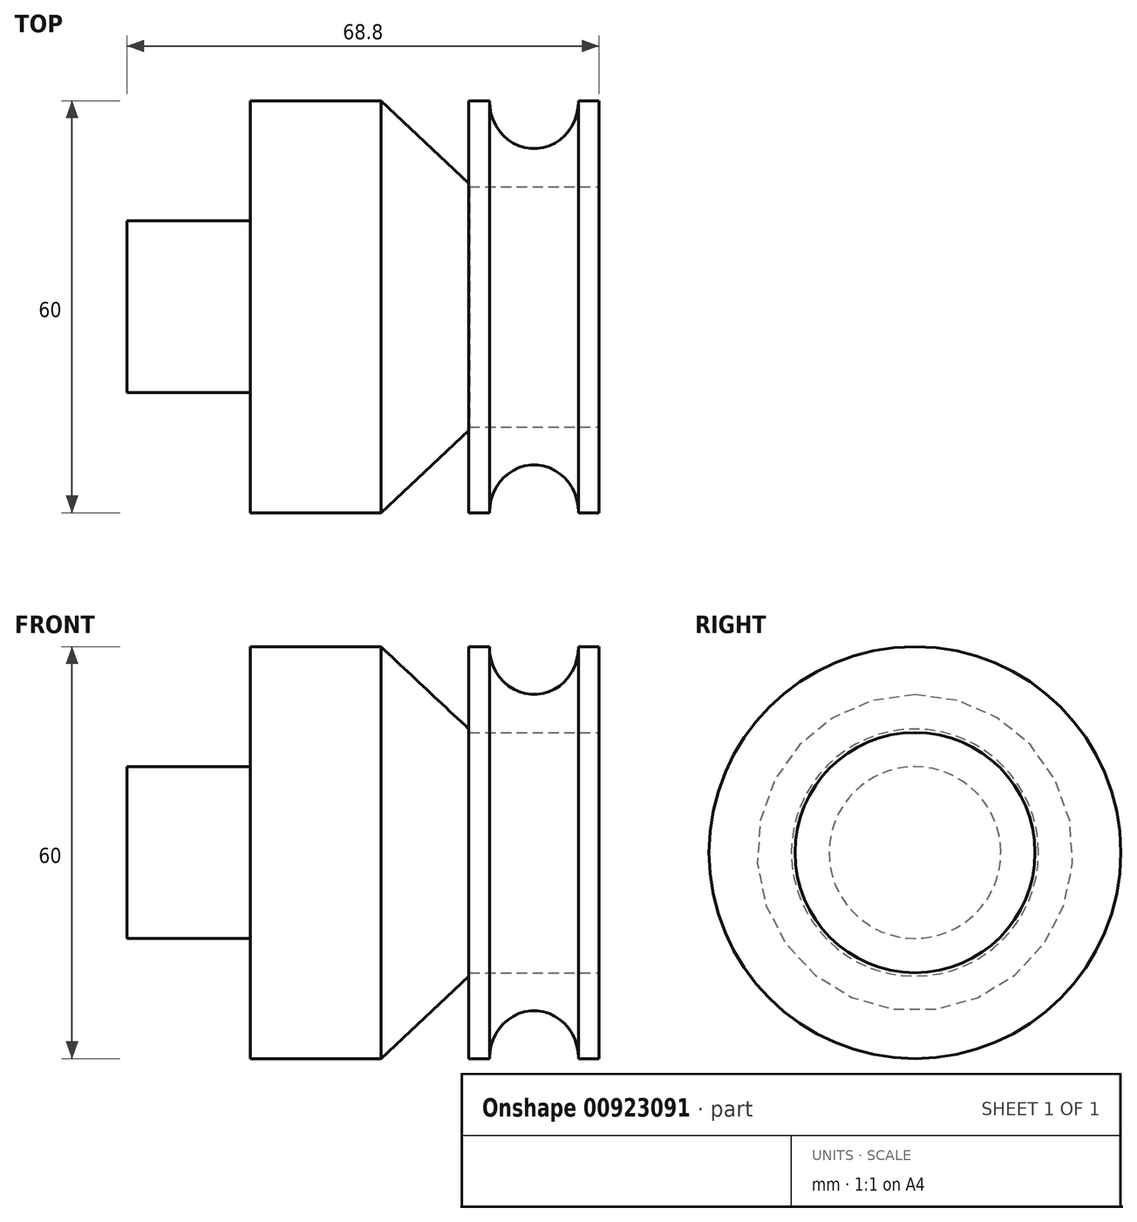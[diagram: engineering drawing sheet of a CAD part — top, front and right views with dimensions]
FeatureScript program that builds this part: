
annotation { "Feature Type Name" : "Feature", "Feature Type Description" : "" }
export const myFeature = defineFeature(function(context is Context, id is Id, definition is map)
    precondition{}
    {
        {
            var Q0;
            Q0=qCreatedBy(makeId("Front.planeOp"),FACE);
            var sketch = newSketch(context, id + "F0", { "sketchPlane" : qUnion([Q0])});
            skLineSegment(sketch, "E0", {"start": v(-12.2, 0) * mm, "end": v(-12.2, 30) * mm});
            skLineSegment(sketch, "E1", {"start": v(6.8, 0) * mm, "end": v(6.8, 30) * mm});
            skLineSegment(sketch, "E2", {"start": v(-12.2, 30) * mm, "end": v(-9.2, 30) * mm});
            skLineSegment(sketch, "E3", {"start": v(6.8, 30) * mm, "end": v(3.8, 30) * mm});
            skLineSegment(sketch, "E4", {"start": v(-12.2, 0) * mm, "end": v(6.8, 0) * mm});
            skPoint(sketch, "E5.centerSnap0", {"position": v(-2.7, 0) * mm});
            skEllipticalArc(sketch, "E6", {});
            const initialGuessF0  = {"E6": [-0.0026993720531463625, 0.03, 0, -1, 0.006985, 0.0065, 4.71238898038469, 1.5707963267948966]};
            skSetInitialGuess(sketch, initialGuessF0);
            skSolve(sketch);
        }
        {
            var Q0;
            Q0 = qSketchRegion(id + "F0", true);
            var Q1;
            Q1=sQuery(id+"F0.wireOp",EDGE,"E4");
            revolve(context, id + "F1", {"surfaceOperationType" : NewSurfaceOperationType.NEW, "entities" : qUnion([Q0]), "axis" : qUnion([Q1]), "revolveType" : RevolveType.FULL});
        }
        {
            var Q0;
            Q0=makeQuery(id+"F1.opRevolve","SWEPT_FACE",FACE,{"disambiguationData":[OSD([sQuery(id+"F0.wireOp",EDGE,"E1")])]});
            var sketch = newSketch(context, id + "F2", { "sketchPlane" : qUnion([Q0])});
            skCircle(sketch, "E7", {"center": v(0, 0) * mm, "radius": 17.48 * mm});
            skSolve(sketch);
        }
        {
            var Q0;
            Q0=makeQuery(id+"F2.imprint","IMPRINT",FACE,{"disambiguationData":[TD([[makeQuery(id+"F2.imprint","IMPRINT",EDGE,{"derivedFrom":sQuery(id+"F2.wireOp",EDGE,"E7")}),1.0]])]});
            var Q1;
            Q1=makeQuery(id+"F1.opRevolve","SWEPT_FACE",FACE,{"disambiguationData":[OSD([sQuery(id+"F0.wireOp",EDGE,"E0")])]});
            extrude(context, id + "F3", {"entities" : qUnion([Q0]), "operationType" : NewBodyOperationType.REMOVE, "oppositeDirection" : true, "depth" : 18.9 * mm, "endBoundEntityFace" : qUnion([Q1]), "offsetDistance" : 25 * mm});
        }
        {
            var Q0;
            Q0=makeQuery(id+"F1.opRevolve","SWEPT_FACE",FACE,{"disambiguationData":[OSD([sQuery(id+"F0.wireOp",EDGE,"E0")])]});
            var sketch = newSketch(context, id + "F4", { "sketchPlane" : qUnion([Q0])});
            skCircle(sketch, "E8", {"center": v(0, 0) * mm, "radius": 18 * mm});
            skSolve(sketch);
        }
        {
            var Q0;
            Q0=qCreatedBy(makeId("Right.planeOp"),FACE);
            cPlane(context, id + "F5", {"entities" : qUnion([Q0]), "cplaneType" : CPlaneType.OFFSET, "offset" : 25 * mm, "oppositeDirection" : true, "width" : 150 * mm, "height" : 150 * mm});
        }
        {
            var Q0;
            Q0=qCreatedBy(id+"F5.planeOp",FACE);
            var sketch = newSketch(context, id + "F6", { "sketchPlane" : qUnion([Q0])});
            skCircle(sketch, "E9", {"center": v(0, 0) * mm, "radius": 30 * mm});
            skSolve(sketch);
        }
        {
            var Q1;
            Q1=makeQuery(id+"F6.imprint","IMPRINT",FACE,{"disambiguationData":[TD([[makeQuery(id+"F6.imprint","IMPRINT",EDGE,{"derivedFrom":sQuery(id+"F6.wireOp",EDGE,"E9")}),1.0]])]});
            var Q2;
            Q2=makeQuery(id+"F4.imprint","IMPRINT",FACE,{"disambiguationData":[TD([[makeQuery(id+"F4.imprint","IMPRINT",EDGE,{"derivedFrom":sQuery(id+"F4.wireOp",EDGE,"E8")}),1.0]])]});
            loft(context, id + "F7", {"operationType" : NewBodyOperationType.ADD, "sheetProfilesArray" : [{ "sheetProfileEntities" : qUnion([Q1]) }, { "sheetProfileEntities" : qUnion([Q2]) }]});
        }
        {
            var Q0;
            Q0=makeQuery(id+"F7.opLoft","CAP_FACE",FACE,{"disambiguationData":[OSD([makeQuery(id+"F6.imprint","IMPRINT",FACE,{"disambiguationData":[TD([[makeQuery(id+"F6.imprint","IMPRINT",EDGE,{"derivedFrom":sQuery(id+"F6.wireOp",EDGE,"E9")}),1.0]])]})])],"isStart":true});
            extrude(context, id + "F8", {"entities" : qUnion([Q0]), "operationType" : NewBodyOperationType.ADD, "depth" : 19 * mm, "offsetDistance" : 25 * mm});
        }
        {
            var Q0;
            Q0=makeQuery(id+"F8.opExtrude","CAP_FACE",FACE,{"disambiguationData":[OSD([makeQuery(id+"F6.imprint","IMPRINT",FACE,{"disambiguationData":[TD([[makeQuery(id+"F6.imprint","IMPRINT",EDGE,{"derivedFrom":sQuery(id+"F6.wireOp",EDGE,"E9")}),1.0]])]})])],"isStart":false});
            var sketch = newSketch(context, id + "F9", { "sketchPlane" : qUnion([Q0])});
            skCircle(sketch, "E10", {"center": v(0, 0) * mm, "radius": 12.5 * mm});
            skSolve(sketch);
        }
        {
            var Q0;
            Q0 = qSketchRegion(id + "F9", true);
            extrude(context, id + "F10", {"entities" : qUnion([Q0]), "operationType" : NewBodyOperationType.ADD, "depth" : 18 * mm, "offsetDistance" : 25 * mm});
        }
    });
